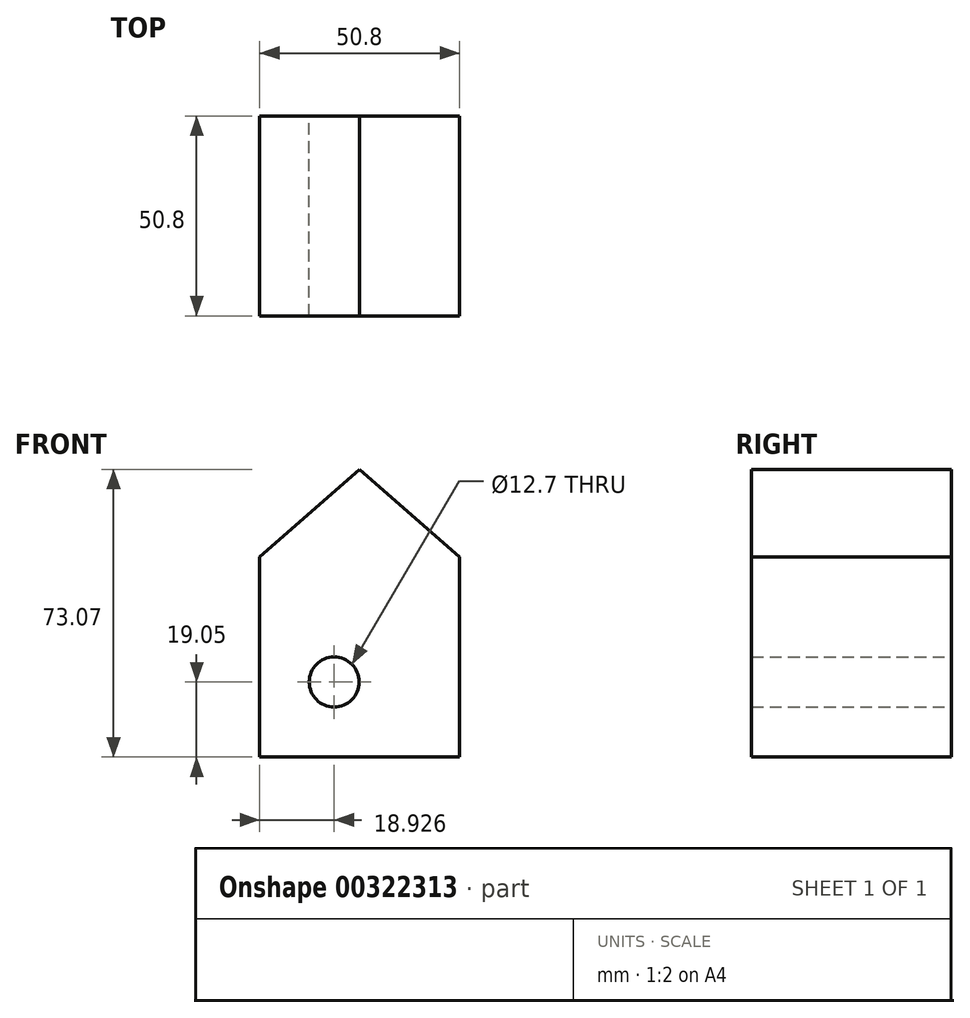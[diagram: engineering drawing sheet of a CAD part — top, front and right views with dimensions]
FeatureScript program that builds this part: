
annotation { "Feature Type Name" : "Feature", "Feature Type Description" : "" }
export const myFeature = defineFeature(function(context is Context, id is Id, definition is map)
    precondition{}
    {
        {
            var Q0;
            Q0=qCreatedBy(makeId("Front.planeOp"),FACE);
            var sketch = newSketch(context, id + "F0", { "sketchPlane" : qUnion([Q0])});
            skLineSegment(sketch, "E0.bottom", {"start": v(25.4, -25.4) * mm, "end": v(-25.4, -25.4) * mm});
            skLineSegment(sketch, "E0.left", {"start": v(25.4, -25.4) * mm, "end": v(25.4, 25.4) * mm});
            skLineSegment(sketch, "E0.right", {"start": v(-25.4, -25.4) * mm, "end": v(-25.4, 25.4) * mm});
            skPoint(sketch, "E0.middle", {"position": v(0, 0) * mm});
            skLineSegment(sketch, "E1", {"start": v(-25.4, 25.4) * mm, "end": v(0, 47.67) * mm});
            skLineSegment(sketch, "E2", {"start": v(25.4, 25.4) * mm, "end": v(0, 47.67) * mm});
            skLineSegment(sketch, "E3.0", {"start": v(-25.52, -25.4) * mm, "end": v(-25.52, 25.4) * mm});
            skCircle(sketch, "E4", {"center": v(-6.47, -6.35) * mm, "radius": 6.35 * mm});
            skSolve(sketch);
        }
        {
            var Q0;
            Q0=makeQuery(id+"F0.imprint","IMPRINT",FACE,{"disambiguationData":[TD([[makeQuery(id+"F0.imprint","IMPRINT",EDGE,{"derivedFrom":sQuery(id+"F0.wireOp",EDGE,"E0.bottom")}),-1.0]])]});
            extrude(context, id + "F1", {"entities" : qUnion([Q0]), "depth" : 50.8 * mm});
        }
    });
